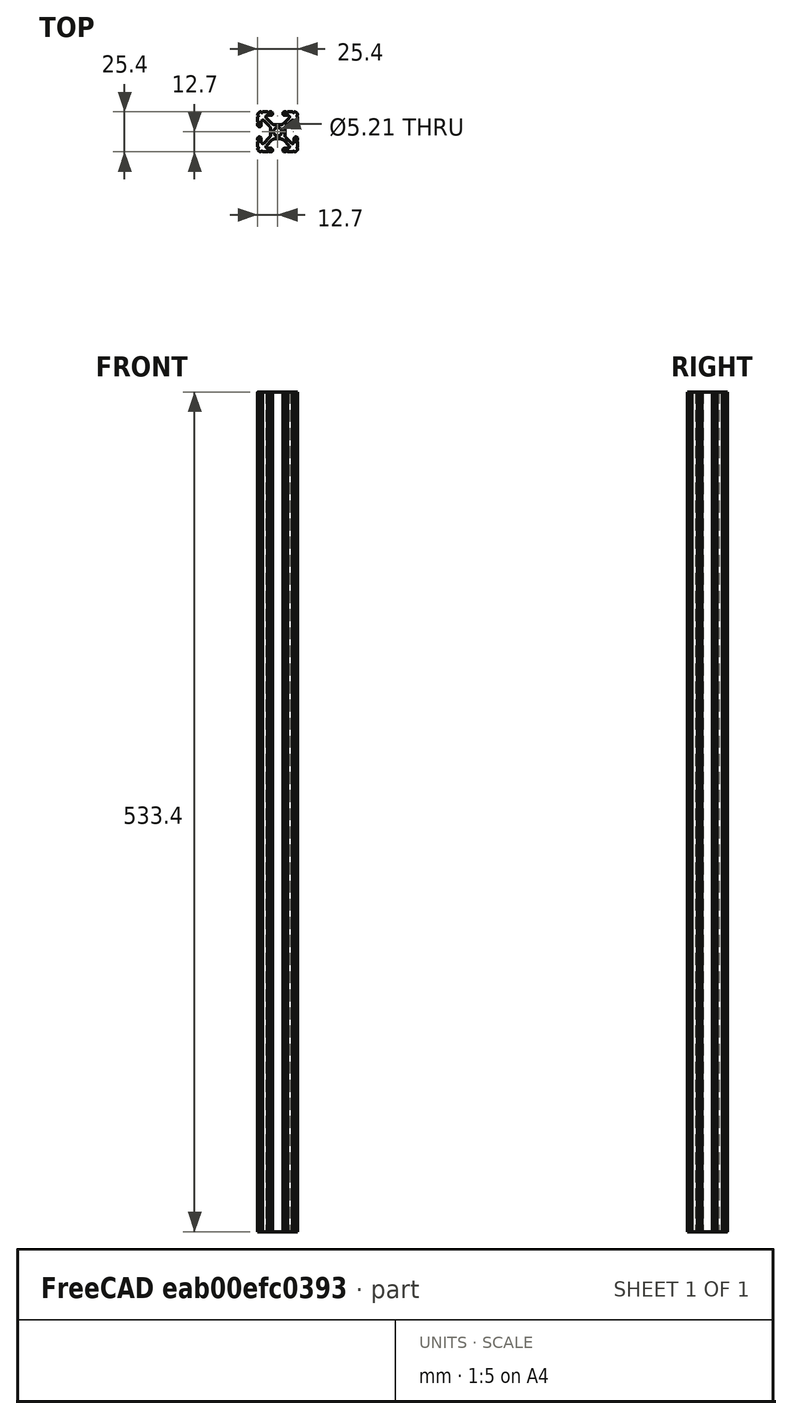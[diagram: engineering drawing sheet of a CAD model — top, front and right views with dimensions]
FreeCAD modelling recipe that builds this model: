
FCSTD DOCUMENT  (FreeCAD 0.19R24267 (Git))
Label: 1010-21
License: All rights reserved
LicenseURL: http://en.wikipedia.org/wiki/All_rights_reserved
objects: Sketcher::SketchObject×1, Part::Extrusion×1
note: 2 computed .brp shape members not serialized (recipe doc carries the construction recipe); baked Part::Feature solids carry a one-line shape summary decoded from their .brp

FEATURE [Sketcher::SketchObject] Sketch097
  FullyConstrained = false
  sketch-geometry (97):
    g0: Circle CenterX=0 CenterY=0 CenterZ=0 NormalX=0 NormalY=0 NormalZ=-1 AngleXU=0 Radius=2.6035
    g1: ArcOfCircle CenterX=12.7 CenterY=5.82508 CenterZ=0 NormalX=0 NormalY=0 NormalZ=1 AngleXU=0 Radius=0.508 StartAngle=1.5708 EndAngle=4.71239
    g2: LineSegment StartX=3.2385 StartY=11.651 StartZ=0 EndX=3.2385 EndY=11.5392 EndZ=0
    g3: LineSegment StartX=6.33313 StartY=-12.7 StartZ=0 EndX=9.55044 EndY=-12.7 EndZ=0
    g4: LineSegment StartX=7.20704 StartY=8.72437 StartZ=0 EndX=3.89827 EndY=5.42317 EndZ=0
    g5: ArcOfCircle CenterX=7.6835 CenterY=1.59319 CenterZ=0 NormalX=0 NormalY=0 NormalZ=1 AngleXU=0 Radius=3.175 StartAngle=2.35505 EndAngle=3.14159
    g6: ArcOfCircle CenterX=-1.70925 CenterY=-7.6708 CenterZ=0 NormalX=0 NormalY=0 NormalZ=1 AngleXU=0 Radius=3.175 StartAngle=1.5708 EndAngle=2.35528
    g7: ArcOfCircle CenterX=11.5392 CenterY=-4.28747 CenterZ=0 NormalX=0 NormalY=0 NormalZ=1 AngleXU=0 Radius=1.04901 StartAngle=1.5708 EndAngle=3.14159
    g8: ArcOfCircle CenterX=12.7 CenterY=-5.82508 CenterZ=0 NormalX=0 NormalY=0 NormalZ=1 AngleXU=0 Radius=0.508 StartAngle=1.5708 EndAngle=4.71239
    g9: LineSegment StartX=4.28751 StartY=10.4902 StartZ=0 EndX=6.47679 EndY=10.4902 EndZ=0
    g10: ArcOfCircle CenterX=4.28751 CenterY=11.651 CenterZ=0 NormalX=0 NormalY=0 NormalZ=1 AngleXU=0 Radius=1.04901 StartAngle=1.5708 EndAngle=3.14159
    g11: ArcOfCircle CenterX=6.47679 CenterY=9.45629 CenterZ=0 NormalX=0 NormalY=0 NormalZ=1 AngleXU=0 Radius=1.03391 StartAngle=5.49664 EndAngle=7.85398
    g12: ArcOfCircle CenterX=4.28751 CenterY=11.5392 CenterZ=0 NormalX=0 NormalY=0 NormalZ=1 AngleXU=0 Radius=1.04901 StartAngle=3.14159 EndAngle=4.71239
    g13: LineSegment StartX=3.95227 StartY=-5.42369 StartZ=0 EndX=7.17965 EndY=-8.64519 EndZ=0
    g14: ArcOfCircle CenterX=11.651 CenterY=4.28747 CenterZ=0 NormalX=0 NormalY=0 NormalZ=1 AngleXU=0 Radius=1.04901 StartAngle=4.71239 EndAngle=6.28319
    g15: ArcOfCircle CenterX=-5.82513 CenterY=-12.7 CenterZ=0 NormalX=0 NormalY=0 NormalZ=1 AngleXU=0 Radius=0.508 StartAngle=0 EndAngle=3.14159
    g16: LineSegment StartX=-6.47679 StartY=10.4902 StartZ=0 EndX=-4.28751 EndY=10.4902 EndZ=0
    g17: ArcOfCircle CenterX=-12.7 CenterY=10.0584 CenterZ=0 NormalX=0 NormalY=0 NormalZ=1 AngleXU=0 Radius=0.508 StartAngle=4.71239 EndAngle=7.85368
    g18: ArcOfCircle CenterX=-12.7 CenterY=5.82508 CenterZ=0 NormalX=0 NormalY=0 NormalZ=1 AngleXU=0 Radius=0.508 StartAngle=4.71239 EndAngle=7.85398
    g19: LineSegment StartX=-11.5392 StartY=-3.23846 StartZ=0 EndX=-11.651 EndY=-3.23846 EndZ=0
    g20: LineSegment StartX=-3.89827 StartY=5.42317 StartZ=0 EndX=-7.20704 EndY=8.72437 EndZ=0
    g21: LineSegment StartX=1.65578 StartY=4.4958 StartZ=0 EndX=-1.65578 EndY=4.4958 EndZ=0
    g22: ArcOfCircle CenterX=-1.65578 CenterY=7.6708 CenterZ=0 NormalX=0 NormalY=0 NormalZ=1 AngleXU=0 Radius=3.175 StartAngle=3.92813 EndAngle=4.71239
    g23: LineSegment StartX=-9.55044 StartY=-12.7 StartZ=0 EndX=-6.33313 EndY=-12.7 EndZ=0
    g24: ArcOfCircle CenterX=-5.82513 CenterY=12.7 CenterZ=0 NormalX=0 NormalY=0 NormalZ=1 AngleXU=0 Radius=0.508 StartAngle=3.14159 EndAngle=6.28319
    g25: ArcOfCircle CenterX=-4.28751 CenterY=11.651 CenterZ=0 NormalX=0 NormalY=0 NormalZ=1 AngleXU=0 Radius=1.04901 StartAngle=0 EndAngle=1.5708
    g26: LineSegment StartX=-12.7 StartY=-4.28747 StartZ=0 EndX=-12.7 EndY=-5.31708 EndZ=0
    g27: ArcOfCircle CenterX=-6.47679 CenterY=9.45629 CenterZ=0 NormalX=0 NormalY=0 NormalZ=1 AngleXU=0 Radius=1.03391 StartAngle=1.5708 EndAngle=3.92813
    g28: ArcOfCircle CenterX=-4.28751 CenterY=11.5392 CenterZ=0 NormalX=0 NormalY=0 NormalZ=1 AngleXU=0 Radius=1.04901 StartAngle=4.71239 EndAngle=6.28319
    g29: LineSegment StartX=-5.44101 StartY=-3.84082 StartZ=0 EndX=-8.73713 EndY=-7.12941 EndZ=0
    g30: ArcOfCircle CenterX=-7.6835 CenterY=-1.59319 CenterZ=0 NormalX=0 NormalY=0 NormalZ=1 AngleXU=0 Radius=3.175 StartAngle=5.49664 EndAngle=6.28319
    g31: LineSegment StartX=-12.7 StartY=5.31708 StartZ=0 EndX=-12.7 EndY=4.28747 EndZ=0
    g32: LineSegment StartX=-8.73713 StartY=7.12941 StartZ=0 EndX=-5.44101 EndY=3.84082 EndZ=0
    g33: LineSegment StartX=-11.651 StartY=3.23846 StartZ=0 EndX=-11.5392 EndY=3.23846 EndZ=0
    g34: ArcOfCircle CenterX=-9.46279 CenterY=-6.40209 CenterZ=0 NormalX=0 NormalY=0 NormalZ=1 AngleXU=0 Radius=1.02741 StartAngle=3.14159 EndAngle=5.49664
    g35: ArcOfCircle CenterX=-10.5918 CenterY=10.5918 CenterZ=0 NormalX=0 NormalY=0 NormalZ=1 AngleXU=0 Radius=2.1082 StartAngle=1.55877 EndAngle=3.15364
    g36: LineSegment StartX=-12.7 StartY=9.5504 StartZ=0 EndX=-12.7 EndY=6.33308 EndZ=0
    g37: LineSegment StartX=-6.33313 StartY=12.7 StartZ=0 EndX=-9.55044 EndY=12.7 EndZ=0
    g38: ArcOfCircle CenterX=-11.5392 CenterY=-4.28747 CenterZ=0 NormalX=0 NormalY=0 NormalZ=1 AngleXU=0 Radius=1.04901 StartAngle=0 EndAngle=1.5708
    g39: LineSegment StartX=4.28751 StartY=-12.7 StartZ=0 EndX=5.31713 EndY=-12.7 EndZ=0
    g40: LineSegment StartX=5.44101 StartY=3.84082 StartZ=0 EndX=8.73713 EndY=7.12941 EndZ=0
    g41: LineSegment StartX=10.4902 StartY=-4.28747 StartZ=0 EndX=10.4902 EndY=-6.40209 EndZ=0
    g42: ArcOfCircle CenterX=9.46279 CenterY=6.40209 CenterZ=0 NormalX=0 NormalY=0 NormalZ=1 AngleXU=0 Radius=1.02741 StartAngle=0 EndAngle=2.35505
    g43: ArcOfCircle CenterX=5.82513 CenterY=-12.7 CenterZ=0 NormalX=0 NormalY=0 NormalZ=1 AngleXU=0 Radius=0.508 StartAngle=0 EndAngle=3.14159
    g44: LineSegment StartX=12.7 StartY=-9.5504 StartZ=0 EndX=12.7 EndY=-6.33308 EndZ=0
    g45: LineSegment StartX=4.5085 StartY=-1.59319 StartZ=0 EndX=4.5085 EndY=1.59319 EndZ=0
    g46: ArcOfCircle CenterX=12.7 CenterY=10.0584 CenterZ=0 NormalX=0 NormalY=0 NormalZ=1 AngleXU=0 Radius=0.508 StartAngle=1.5711 EndAngle=4.71239
    g47: ArcOfCircle CenterX=12.7 CenterY=-10.0584 CenterZ=0 NormalX=0 NormalY=0 NormalZ=1 AngleXU=0 Radius=0.508 StartAngle=1.5708 EndAngle=4.71209
    g48: LineSegment StartX=3.2385 StartY=-11.5392 StartZ=0 EndX=3.2385 EndY=-11.651 EndZ=0
    g49: LineSegment StartX=8.73713 StartY=-7.12941 StartZ=0 EndX=5.44101 EndY=-3.84082 EndZ=0
    g50: ArcOfCircle CenterX=11.651 CenterY=-4.28747 CenterZ=0 NormalX=0 NormalY=0 NormalZ=1 AngleXU=0 Radius=1.04901 StartAngle=0 EndAngle=1.5708
    g51: ArcOfCircle CenterX=1.65578 CenterY=7.6708 CenterZ=0 NormalX=0 NormalY=0 NormalZ=1 AngleXU=0 Radius=3.175 StartAngle=4.71239 EndAngle=5.49664
    g52: ArcOfCircle CenterX=7.6835 CenterY=-1.59319 CenterZ=0 NormalX=0 NormalY=0 NormalZ=1 AngleXU=0 Radius=3.175 StartAngle=3.14159 EndAngle=3.92813
    g53: LineSegment StartX=12.7 StartY=4.28747 StartZ=0 EndX=12.7 EndY=5.31708 EndZ=0
    g54: ArcOfCircle CenterX=6.41641 CenterY=-9.40983 CenterZ=0 NormalX=0 NormalY=0 NormalZ=1 AngleXU=0 Radius=1.08037 StartAngle=4.71239 EndAngle=7.06949
    g55: LineSegment StartX=12.7 StartY=-5.31708 StartZ=0 EndX=12.7 EndY=-4.28747 EndZ=0
    g56: ArcOfCircle CenterX=10.0584 CenterY=-12.7 CenterZ=0 NormalX=0 NormalY=0 NormalZ=1 AngleXU=0 Radius=0.508 StartAngle=0.000300194 EndAngle=3.14159
    g57: ArcOfCircle CenterX=11.5392 CenterY=4.28747 CenterZ=0 NormalX=0 NormalY=0 NormalZ=1 AngleXU=0 Radius=1.04901 StartAngle=3.14159 EndAngle=4.71239
    g58: LineSegment StartX=12.7 StartY=6.33308 StartZ=0 EndX=12.7 EndY=9.5504 EndZ=0
    g59: ArcOfCircle CenterX=4.28751 CenterY=-11.5392 CenterZ=0 NormalX=0 NormalY=0 NormalZ=1 AngleXU=0 Radius=1.04901 StartAngle=1.5708 EndAngle=3.14159
    g60: ArcOfCircle CenterX=10.5918 CenterY=10.5918 CenterZ=0 NormalX=0 NormalY=0 NormalZ=1 AngleXU=0 Radius=2.1082 StartAngle=6.27114 EndAngle=7.86601
    g61: ArcOfCircle CenterX=9.46279 CenterY=-6.40209 CenterZ=0 NormalX=0 NormalY=0 NormalZ=1 AngleXU=0 Radius=1.02741 StartAngle=3.92813 EndAngle=6.28319
    g62: LineSegment StartX=6.41641 StartY=-10.4902 StartZ=0 EndX=4.28751 EndY=-10.4902 EndZ=0
    g63: LineSegment StartX=-10.4902 StartY=-6.40209 StartZ=0 EndX=-10.4902 EndY=-4.28747 EndZ=0
    g64: ArcOfCircle CenterX=-9.46279 CenterY=6.40209 CenterZ=0 NormalX=0 NormalY=0 NormalZ=1 AngleXU=0 Radius=1.02741 StartAngle=0.786542 EndAngle=3.14159
    g65: LineSegment StartX=-10.4902 StartY=4.28747 StartZ=0 EndX=-10.4902 EndY=6.40209 EndZ=0
    g66: LineSegment StartX=-4.5085 StartY=1.59319 StartZ=0 EndX=-4.5085 EndY=-1.59319 EndZ=0
    g67: LineSegment StartX=-4.28751 StartY=12.7 StartZ=0 EndX=-5.31713 EndY=12.7 EndZ=0
    g68: ArcOfCircle CenterX=-11.5392 CenterY=4.28747 CenterZ=0 NormalX=0 NormalY=0 NormalZ=1 AngleXU=0 Radius=1.04901 StartAngle=4.71239 EndAngle=6.28319
    g69: LineSegment StartX=-3.2385 StartY=11.5392 StartZ=0 EndX=-3.2385 EndY=11.651 EndZ=0
    g70: ArcOfCircle CenterX=-11.651 CenterY=4.28747 CenterZ=0 NormalX=0 NormalY=0 NormalZ=1 AngleXU=0 Radius=1.04901 StartAngle=3.14159 EndAngle=4.71239
    g71: ArcOfCircle CenterX=-7.6835 CenterY=1.59319 CenterZ=0 NormalX=0 NormalY=0 NormalZ=1 AngleXU=0 Radius=3.175 StartAngle=0 EndAngle=0.786542
    g72: ArcOfCircle CenterX=-10.0584 CenterY=12.7 CenterZ=0 NormalX=0 NormalY=0 NormalZ=1 AngleXU=0 Radius=0.508 StartAngle=3.14189 EndAngle=6.28319
    g73: LineSegment StartX=-1.70925 StartY=-4.4958 StartZ=0 EndX=1.70925 EndY=-4.4958 EndZ=0
    g74: LineSegment StartX=11.651 StartY=-3.23846 StartZ=0 EndX=11.5392 EndY=-3.23846 EndZ=0
    g75: ArcOfCircle CenterX=-10.5918 CenterY=-10.5918 CenterZ=0 NormalX=0 NormalY=0 NormalZ=1 AngleXU=0 Radius=2.1082 StartAngle=3.12954 EndAngle=4.72442
    g76: ArcOfCircle CenterX=10.5918 CenterY=-10.5918 CenterZ=0 NormalX=0 NormalY=0 NormalZ=1 AngleXU=0 Radius=2.1082 StartAngle=4.70036 EndAngle=6.29523
    g77: ArcOfCircle CenterX=-12.7 CenterY=-5.82508 CenterZ=0 NormalX=0 NormalY=0 NormalZ=1 AngleXU=0 Radius=0.508 StartAngle=4.71239 EndAngle=7.85398
    g78: ArcOfCircle CenterX=5.82513 CenterY=12.7 CenterZ=0 NormalX=0 NormalY=0 NormalZ=1 AngleXU=0 Radius=0.508 StartAngle=3.14159 EndAngle=6.28319
    g79: LineSegment StartX=9.55044 StartY=12.7 StartZ=0 EndX=6.33313 EndY=12.7 EndZ=0
    g80: ArcOfCircle CenterX=10.0584 CenterY=12.7 CenterZ=0 NormalX=0 NormalY=0 NormalZ=1 AngleXU=0 Radius=0.508 StartAngle=3.14159 EndAngle=6.28289
    g81: ArcOfCircle CenterX=1.70925 CenterY=-7.6708 CenterZ=0 NormalX=0 NormalY=0 NormalZ=1 AngleXU=0 Radius=3.175 StartAngle=0.78631 EndAngle=1.5708
    g82: ArcOfCircle CenterX=4.28751 CenterY=-11.651 CenterZ=0 NormalX=0 NormalY=0 NormalZ=1 AngleXU=0 Radius=1.04901 StartAngle=3.14159 EndAngle=4.71239
    g83: LineSegment StartX=5.31713 StartY=12.7 StartZ=0 EndX=4.28751 EndY=12.7 EndZ=0
    g84: LineSegment StartX=10.4902 StartY=6.40209 StartZ=0 EndX=10.4902 EndY=4.28747 EndZ=0
    g85: LineSegment StartX=11.5392 StartY=3.23846 StartZ=0 EndX=11.651 EndY=3.23846 EndZ=0
    g86: ArcOfCircle CenterX=-10.0584 CenterY=-12.7 CenterZ=0 NormalX=0 NormalY=0 NormalZ=1 AngleXU=0 Radius=0.508 StartAngle=0 EndAngle=3.14129
    g87: ArcOfCircle CenterX=-12.7 CenterY=-10.0584 CenterZ=0 NormalX=0 NormalY=0 NormalZ=1 AngleXU=0 Radius=0.508 StartAngle=4.71269 EndAngle=7.85398
    g88: ArcOfCircle CenterX=-4.28751 CenterY=-11.5392 CenterZ=0 NormalX=0 NormalY=0 NormalZ=1 AngleXU=0 Radius=1.04901 StartAngle=0 EndAngle=1.5708
    g89: ArcOfCircle CenterX=-4.28751 CenterY=-11.651 CenterZ=0 NormalX=0 NormalY=0 NormalZ=1 AngleXU=0 Radius=1.04901 StartAngle=4.71239 EndAngle=6.28319
    g90: LineSegment StartX=-12.7 StartY=-6.33308 StartZ=0 EndX=-12.7 EndY=-9.5504 EndZ=0
    g91: ArcOfCircle CenterX=-11.651 CenterY=-4.28747 CenterZ=0 NormalX=0 NormalY=0 NormalZ=1 AngleXU=0 Radius=1.04901 StartAngle=1.5708 EndAngle=3.14159
    g92: LineSegment StartX=-7.17965 StartY=-8.64519 StartZ=0 EndX=-3.95227 EndY=-5.42369 EndZ=0
    g93: LineSegment StartX=-5.31713 StartY=-12.7 StartZ=0 EndX=-4.28751 EndY=-12.7 EndZ=0
    g94: LineSegment StartX=-3.2385 StartY=-11.651 StartZ=0 EndX=-3.2385 EndY=-11.5392 EndZ=0
    g95: ArcOfCircle CenterX=-6.41641 CenterY=-9.40983 CenterZ=0 NormalX=0 NormalY=0 NormalZ=1 AngleXU=0 Radius=1.08037 StartAngle=2.35528 EndAngle=4.71239
    g96: LineSegment StartX=-4.28751 StartY=-10.4902 StartZ=0 EndX=-6.41641 EndY=-10.4902 EndZ=0
FEATURE [Part::Extrusion] Extrude
  Base = -> Sketch097
  Dir = (0,0,1)
  DirMode = 2
  FaceMakerClass = Part::FaceMakerBullseye
  LengthFwd = 533.4
  LengthRev = 0
  Solid = true
  Symmetric = false
